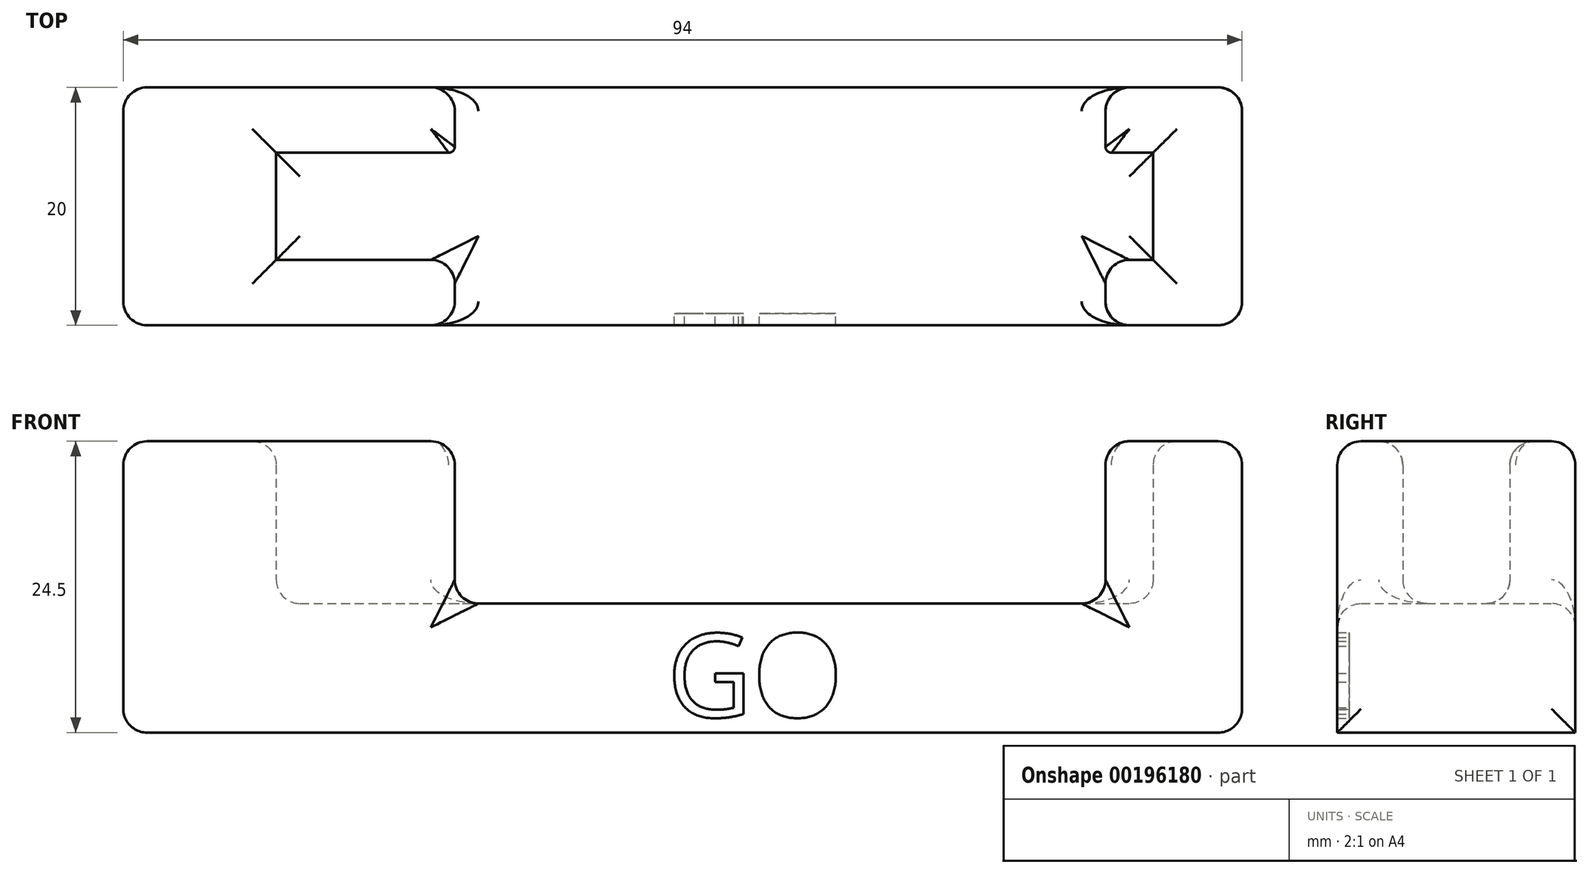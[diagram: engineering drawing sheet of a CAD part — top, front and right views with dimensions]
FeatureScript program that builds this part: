
annotation { "Feature Type Name" : "Feature", "Feature Type Description" : "" }
export const myFeature = defineFeature(function(context is Context, id is Id, definition is map)
    precondition{}
    {
        {
            var Q0;
            Q0=qCreatedBy(makeId("Front.planeOp"),FACE);
            var sketch = newSketch(context, id + "F0", { "sketchPlane" : qUnion([Q0])});
            skLineSegment(sketch, "E0.bottom", {"start": v(-9.82, 14.1) * mm, "end": v(84.18, 14.1) * mm});
            skLineSegment(sketch, "E0.left", {"start": v(-9.82, 14.1) * mm, "end": v(-9.82, -10.4) * mm});
            skLineSegment(sketch, "E0.right", {"start": v(84.18, 14.1) * mm, "end": v(84.18, -10.4) * mm});
            skLineSegment(sketch, "E1.top", {"start": v(3.03, 0.45) * mm, "end": v(76.7, 0.45) * mm});
            skLineSegment(sketch, "E1.left", {"start": v(3.03, 14.1) * mm, "end": v(3.03, 0.45) * mm});
            skLineSegment(sketch, "E1.right", {"start": v(76.7, 14.1) * mm, "end": v(76.7, 0.45) * mm});
            skText(sketch, "E2", { "text": "    GO", "fontName": "OpenSans-Regular.ttf"});
            skLineSegment(sketch, "E3", {"start": v(18.03, 14.1) * mm, "end": v(18.03, 0.45) * mm});
            skLineSegment(sketch, "E4", {"start": v(72.7, 14.1) * mm, "end": v(72.7, 0.45) * mm});
            skLineSegment(sketch, "E5", {"start": v(-9.82, -10.4) * mm, "end": v(84.18, -10.4) * mm});
            const initialGuessF0  = {"E2": [0.02568, -0.0091, 1, 0, 0.00706]};
            skSetInitialGuess(sketch, initialGuessF0);
            skSolve(sketch);
        }
        {
            var Q0;
            {var subQ3=sQuery(id+"F0.wireOp",EDGE,"E0.left");Q0=makeQuery(id+"F0.imprint","IMPRINT",FACE,{"disambiguationData":[TD([[makeQuery(id+"F0.imprint","IMPRINT",EDGE,{"derivedFrom":subQ3}),1.0]])]});}
            extrude(context, id + "F1", {"entities" : qUnion([Q0]), "depth" : 20 * mm});
        }
        {
            var Q0;
            Q0=makeQuery(id+"F0.imprint","IMPRINT",FACE,{"disambiguationData":[TD([[makeQuery(id+"F0.imprint","IMPRINT",EDGE,{"derivedFrom":sQuery(id+"F0.wireOp",EDGE,"E2.sketch_text.stroke-51")}),-1.0]])]});
            var Q1;
            Q1=makeQuery(id+"F0.imprint","IMPRINT",FACE,{"disambiguationData":[TD([[makeQuery(id+"F0.imprint","IMPRINT",EDGE,{"derivedFrom":sQuery(id+"F0.wireOp",EDGE,"E2.sketch_text.stroke-67")}),-1.0]])]});
            var Q2;
            Q2=makeQuery(id+"F0.imprint","IMPRINT",FACE,{"disambiguationData":[TD([[makeQuery(id+"F0.imprint","IMPRINT",EDGE,{"derivedFrom":sQuery(id+"F0.wireOp",EDGE,"E2.sketch_text.stroke-71")}),-1.0]])]});
            var Q3;
            Q3=makeQuery(id+"F0.imprint","IMPRINT",FACE,{"disambiguationData":[TD([[makeQuery(id+"F0.imprint","IMPRINT",EDGE,{"derivedFrom":sQuery(id+"F0.wireOp",EDGE,"E2.sketch_text.stroke-91")}),-1.0]])]});
            var Q4;
            Q4=makeQuery(id+"F0.imprint","IMPRINT",FACE,{"disambiguationData":[TD([[makeQuery(id+"F0.imprint","IMPRINT",EDGE,{"derivedFrom":sQuery(id+"F0.wireOp",EDGE,"E2.sketch_text.stroke-36")}),-1.0]])]});
            var Q5;
            Q5=makeQuery(id+"F0.imprint","IMPRINT",FACE,{"disambiguationData":[TD([[makeQuery(id+"F0.imprint","IMPRINT",EDGE,{"derivedFrom":sQuery(id+"F0.wireOp",EDGE,"E2.sketch_text.stroke-0")}),-1.0]])]});
            var Q6;
            Q6=makeQuery(id+"F0.imprint","IMPRINT",FACE,{"disambiguationData":[TD([[makeQuery(id+"F0.imprint","IMPRINT",EDGE,{"derivedFrom":sQuery(id+"F0.wireOp",EDGE,"E2.sketch_text.stroke-20")}),-1.0]])]});
            var Q7;
            Q7=makeQuery(id+"F0.imprint","IMPRINT",FACE,{"disambiguationData":[TD([[makeQuery(id+"F0.imprint","IMPRINT",EDGE,{"derivedFrom":sQuery(id+"F0.wireOp",EDGE,"E2.sketch_text.stroke-28")}),1.0]])]});
            var Q8;
            Q8=makeQuery(id+"F0.imprint","IMPRINT",FACE,{"disambiguationData":[TD([[makeQuery(id+"F0.imprint","IMPRINT",EDGE,{"derivedFrom":sQuery(id+"F0.wireOp",EDGE,"E2.sketch_text.stroke-99")}),1.0]])]});
            var Q9;
            Q9=makeQuery(id+"F0.imprint","IMPRINT",FACE,{"disambiguationData":[TD([[makeQuery(id+"F0.imprint","IMPRINT",EDGE,{"derivedFrom":sQuery(id+"F0.wireOp",EDGE,"E2.sketch_text.stroke-59")}),1.0]])]});
            extrude(context, id + "F2", {"entities" : qUnion([Q0, Q1, Q2, Q3, Q4, Q5, Q6, Q7, Q8, Q9]), "operationType" : NewBodyOperationType.ADD, "depth" : 19 * mm});
        }
        {
            var Q0;
            {var subQ0=sQuery(id+"F0.wireOp",EDGE,"E1.left");Q0=makeQuery(id+"F0.imprint","IMPRINT",FACE,{"disambiguationData":[TD([[makeQuery(id+"F0.imprint","IMPRINT",EDGE,{"derivedFrom":subQ0}),1.0]])]});}
            var Q1;
            {var subQ0=sQuery(id+"F0.wireOp",EDGE,"E1.right");Q1=makeQuery(id+"F0.imprint","IMPRINT",FACE,{"disambiguationData":[TD([[makeQuery(id+"F0.imprint","IMPRINT",EDGE,{"derivedFrom":subQ0}),-1.0]])]});}
            var Q2;
            {var subQ0=sQuery(id+"F0.wireOp",EDGE,"2L4el6af-6clv-Qu9y-48nY-g4NLMY6r5mmJ.left");Q2=makeQuery(id+"F0.imprint","IMPRINT",FACE,{"disambiguationData":[TD([[makeQuery(id+"F0.imprint","IMPRINT",EDGE,{"derivedFrom":subQ0}),1.0]])]});}
            var Q3;
            {var subQ0=sQuery(id+"F0.wireOp",EDGE,"2L4el6af-6clv-Qu9y-48nY-g4NLMY6r5mmJ.right");Q3=makeQuery(id+"F0.imprint","IMPRINT",FACE,{"disambiguationData":[TD([[makeQuery(id+"F0.imprint","IMPRINT",EDGE,{"derivedFrom":subQ0}),-1.0]])]});}
            extrude(context, id + "F3", {"entities" : qUnion([Q0, Q1, Q2, Q3]), "operationType" : NewBodyOperationType.ADD, "depth" : 20 * mm});
        }
        {
            var Q0;
            {var subQ0=sQuery(id+"F0.wireOp",EDGE,"2L4el6af-6clv-Qu9y-48nY-g4NLMY6r5mmJ.left");Q0=makeQuery(id+"F0.imprint","IMPRINT",FACE,{"disambiguationData":[TD([[makeQuery(id+"F0.imprint","IMPRINT",EDGE,{"derivedFrom":subQ0}),1.0]])]});}
            var Q1;
            {var subQ0=sQuery(id+"F0.wireOp",EDGE,"2L4el6af-6clv-Qu9y-48nY-g4NLMY6r5mmJ.right");Q1=makeQuery(id+"F0.imprint","IMPRINT",FACE,{"disambiguationData":[TD([[makeQuery(id+"F0.imprint","IMPRINT",EDGE,{"derivedFrom":subQ0}),-1.0]])]});}
            var Q2;
            {var subQ0=sQuery(id+"F0.wireOp",EDGE,"E1.left");Q2=makeQuery(id+"F0.imprint","IMPRINT",FACE,{"disambiguationData":[TD([[makeQuery(id+"F0.imprint","IMPRINT",EDGE,{"derivedFrom":subQ0}),1.0]])]});}
            var Q3;
            {var subQ0=sQuery(id+"F0.wireOp",EDGE,"E1.right");Q3=makeQuery(id+"F0.imprint","IMPRINT",FACE,{"disambiguationData":[TD([[makeQuery(id+"F0.imprint","IMPRINT",EDGE,{"derivedFrom":subQ0}),-1.0]])]});}
            extrude(context, id + "F4", {"entities" : qUnion([Q0, Q1, Q2, Q3]), "operationType" : NewBodyOperationType.REMOVE, "depth" : 14.5 * mm, "hasSecondDirection" : true, "secondDirectionOppositeDirection" : false, "secondDirectionDepth" : 5.5 * mm});
        }
        {
            var Q0;
            Q0=makeQuery(id+"F4.boolean.opBoolean","COPY",EDGE,{"derivedFrom":makeQuery(id+"F4.opExtrude","SWEPT_EDGE",EDGE,{"disambiguationData":[OSD([sQuery(id+"F0.wireOp",EDGE,"E0.top"),sQuery(id+"F0.wireOp",EDGE,"2L4el6af-6clv-Qu9y-48nY-g4NLMY6r5mmJ.left")])]})});
            var Q1;
            {var subQ0=sQuery(id+"F0.wireOp",EDGE,"E0.top");Q1=makeQuery(id+"F4.boolean.opBoolean","COPY",EDGE,{"derivedFrom":makeQuery(id+"F4.opExtrude","CAP_EDGE",EDGE,{"disambiguationData":[OSD([subQ0]),TDD([makeQuery(id+"F0.imprint","IMPRINT",EDGE,{"disambiguationData":[TD([[makeQuery(id+"F0.imprint","INTERSECT",VERTEX,{"derivedFrom":[subQ0,sQuery(id+"F0.wireOp",EDGE,"2L4el6af-6clv-Qu9y-48nY-g4NLMY6r5mmJ.left")]}),-1.0]])],"derivedFrom":subQ0})])],"isStart":false})});}
            var Q2;
            {var subQ0=sQuery(id+"F0.wireOp",EDGE,"E0.top");Q2=makeQuery(id+"F4.boolean.opBoolean","COPY",EDGE,{"derivedFrom":makeQuery(id+"F4.opExtrude","CAP_EDGE",EDGE,{"disambiguationData":[OSD([subQ0]),TDD([makeQuery(id+"F0.imprint","IMPRINT",EDGE,{"disambiguationData":[TD([[makeQuery(id+"F0.imprint","INTERSECT",VERTEX,{"derivedFrom":[subQ0,sQuery(id+"F0.wireOp",EDGE,"2L4el6af-6clv-Qu9y-48nY-g4NLMY6r5mmJ.left")]}),-1.0]])],"derivedFrom":subQ0})])],"isStart":true})});}
            var Q3;
            Q3=makeQuery(id+"F4.boolean.opBoolean","COPY",EDGE,{"derivedFrom":makeQuery(id+"F4.opExtrude","CAP_EDGE",EDGE,{"disambiguationData":[OSD([sQuery(id+"F0.wireOp",EDGE,"ZneDm9bx-5IyB-59Bp-oYEK-Q0VNZlboGKRZ")])],"isStart":false})});
            var Q4;
            Q4=makeQuery(id+"F4.boolean.opBoolean","COPY",EDGE,{"derivedFrom":makeQuery(id+"F4.opExtrude","CAP_EDGE",EDGE,{"disambiguationData":[OSD([sQuery(id+"F0.wireOp",EDGE,"ZneDm9bx-5IyB-59Bp-oYEK-Q0VNZlboGKRZ")])],"isStart":true})});
            var Q5;
            {var subQ0=sQuery(id+"F0.wireOp",EDGE,"E0.top");Q5=makeQuery(id+"F4.boolean.opBoolean","COPY",EDGE,{"derivedFrom":makeQuery(id+"F4.opExtrude","CAP_EDGE",EDGE,{"disambiguationData":[OSD([subQ0]),TDD([makeQuery(id+"F0.imprint","IMPRINT",EDGE,{"disambiguationData":[TD([[makeQuery(id+"F0.imprint","INTERSECT",VERTEX,{"derivedFrom":[subQ0,sQuery(id+"F0.wireOp",EDGE,"2L4el6af-6clv-Qu9y-48nY-g4NLMY6r5mmJ.right")]}),1.0]])],"derivedFrom":subQ0})])],"isStart":false})});}
            var Q6;
            Q6=makeQuery(id+"F4.boolean.opBoolean","COPY",EDGE,{"derivedFrom":makeQuery(id+"F4.opExtrude","SWEPT_EDGE",EDGE,{"disambiguationData":[OSD([sQuery(id+"F0.wireOp",EDGE,"E0.top"),sQuery(id+"F0.wireOp",EDGE,"2L4el6af-6clv-Qu9y-48nY-g4NLMY6r5mmJ.right")])]})});
            var Q7;
            {var subQ0=sQuery(id+"F0.wireOp",EDGE,"E0.top");Q7=makeQuery(id+"F4.boolean.opBoolean","COPY",EDGE,{"derivedFrom":makeQuery(id+"F4.opExtrude","CAP_EDGE",EDGE,{"disambiguationData":[OSD([subQ0]),TDD([makeQuery(id+"F0.imprint","IMPRINT",EDGE,{"disambiguationData":[TD([[makeQuery(id+"F0.imprint","INTERSECT",VERTEX,{"derivedFrom":[subQ0,sQuery(id+"F0.wireOp",EDGE,"2L4el6af-6clv-Qu9y-48nY-g4NLMY6r5mmJ.right")]}),1.0]])],"derivedFrom":subQ0})])],"isStart":true})});}
            var Q8;
            Q8=makeQuery(id+"F4.boolean.opBoolean","COPY",EDGE,{"derivedFrom":makeQuery(id+"F4.opExtrude","CAP_EDGE",EDGE,{"disambiguationData":[OSD([sQuery(id+"F0.wireOp",EDGE,"gIBaWbCc-atec-Ogfb-776C-qDHbfGT0BQME")])],"isStart":true})});
            var Q9;
            Q9=makeQuery(id+"F4.boolean.opBoolean","COPY",EDGE,{"derivedFrom":makeQuery(id+"F4.opExtrude","CAP_EDGE",EDGE,{"disambiguationData":[OSD([sQuery(id+"F0.wireOp",EDGE,"gIBaWbCc-atec-Ogfb-776C-qDHbfGT0BQME")])],"isStart":false})});
            var Q10;
            {var subQ0=sQuery(id+"F0.wireOp",EDGE,"E0.bottom");Q10=makeQuery(id+"F4.boolean.opBoolean","COPY",EDGE,{"derivedFrom":makeQuery(id+"F4.opExtrude","CAP_EDGE",EDGE,{"disambiguationData":[OSD([subQ0]),TDD([makeQuery(id+"F0.imprint","IMPRINT",EDGE,{"disambiguationData":[TD([[makeQuery(id+"F0.imprint","INTERSECT",VERTEX,{"derivedFrom":[subQ0,sQuery(id+"F0.wireOp",EDGE,"E1.left")]}),-1.0]])],"derivedFrom":subQ0})])],"isStart":true})});}
            var Q11;
            Q11=makeQuery(id+"F4.boolean.opBoolean","COPY",EDGE,{"derivedFrom":makeQuery(id+"F4.opExtrude","SWEPT_EDGE",EDGE,{"disambiguationData":[OSD([sQuery(id+"F0.wireOp",EDGE,"E0.bottom"),sQuery(id+"F0.wireOp",EDGE,"E1.left")])]})});
            var Q12;
            {var subQ0=sQuery(id+"F0.wireOp",EDGE,"E0.bottom");Q12=makeQuery(id+"F4.boolean.opBoolean","COPY",EDGE,{"derivedFrom":makeQuery(id+"F4.opExtrude","CAP_EDGE",EDGE,{"disambiguationData":[OSD([subQ0]),TDD([makeQuery(id+"F0.imprint","IMPRINT",EDGE,{"disambiguationData":[TD([[makeQuery(id+"F0.imprint","INTERSECT",VERTEX,{"derivedFrom":[subQ0,sQuery(id+"F0.wireOp",EDGE,"E1.left")]}),-1.0]])],"derivedFrom":subQ0})])],"isStart":false})});}
            var Q13;
            {var subQ0=sQuery(id+"F0.wireOp",EDGE,"E0.bottom");Q13=makeQuery(id+"F4.boolean.opBoolean","COPY",EDGE,{"derivedFrom":makeQuery(id+"F4.opExtrude","CAP_EDGE",EDGE,{"disambiguationData":[OSD([subQ0]),TDD([makeQuery(id+"F0.imprint","IMPRINT",EDGE,{"disambiguationData":[TD([[makeQuery(id+"F0.imprint","INTERSECT",VERTEX,{"derivedFrom":[subQ0,sQuery(id+"F0.wireOp",EDGE,"E1.right")]}),1.0]])],"derivedFrom":subQ0})])],"isStart":true})});}
            var Q14;
            Q14=makeQuery(id+"F4.boolean.opBoolean","COPY",EDGE,{"derivedFrom":makeQuery(id+"F4.opExtrude","SWEPT_EDGE",EDGE,{"disambiguationData":[OSD([sQuery(id+"F0.wireOp",EDGE,"E0.bottom"),sQuery(id+"F0.wireOp",EDGE,"E1.right")])]})});
            var Q15;
            {var subQ0=sQuery(id+"F0.wireOp",EDGE,"E0.bottom");Q15=makeQuery(id+"F4.boolean.opBoolean","COPY",EDGE,{"derivedFrom":makeQuery(id+"F4.opExtrude","CAP_EDGE",EDGE,{"disambiguationData":[OSD([subQ0]),TDD([makeQuery(id+"F0.imprint","IMPRINT",EDGE,{"disambiguationData":[TD([[makeQuery(id+"F0.imprint","INTERSECT",VERTEX,{"derivedFrom":[subQ0,sQuery(id+"F0.wireOp",EDGE,"E1.right")]}),1.0]])],"derivedFrom":subQ0})])],"isStart":false})});}
            var Q16;
            Q16=makeQuery(id+"F4.boolean.opBoolean","COPY",EDGE,{"derivedFrom":makeQuery(id+"F4.opExtrude","CAP_EDGE",EDGE,{"disambiguationData":[OSD([sQuery(id+"F0.wireOp",EDGE,"E3")])],"isStart":true})});
            var Q17;
            Q17=makeQuery(id+"F4.boolean.opBoolean","COPY",EDGE,{"derivedFrom":makeQuery(id+"F4.opExtrude","CAP_EDGE",EDGE,{"disambiguationData":[OSD([sQuery(id+"F0.wireOp",EDGE,"E3")])],"isStart":false})});
            var Q18;
            Q18=makeQuery(id+"F4.boolean.opBoolean","COPY",EDGE,{"derivedFrom":makeQuery(id+"F4.opExtrude","CAP_EDGE",EDGE,{"disambiguationData":[OSD([sQuery(id+"F0.wireOp",EDGE,"E4")])],"isStart":true})});
            var Q19;
            Q19=makeQuery(id+"F4.boolean.opBoolean","COPY",EDGE,{"derivedFrom":makeQuery(id+"F4.opExtrude","CAP_EDGE",EDGE,{"disambiguationData":[OSD([sQuery(id+"F0.wireOp",EDGE,"E4")])],"isStart":false})});
            fillet(context, id + "F5", {"entities" : qUnion([Q0, Q1, Q2, Q3, Q4, Q5, Q6, Q7, Q8, Q9, Q10, Q11, Q12, Q13, Q14, Q15, Q16, Q17, Q18, Q19]), "radius" : 0.5 * mm, "tangentPropagation" : true, "allowEdgeOverflow" : false});
        }
        {
            var Q0;
            {var subQ0=sQuery(id+"F0.wireOp",EDGE,"E0.bottom");var subQ1=makeQuery(id+"F0.imprint","INTERSECT",VERTEX,{"derivedFrom":[subQ0,sQuery(id+"F0.wireOp",EDGE,"E1.left")]});Q0=makeQuery(id+"F3.boolean.opBoolean","MERGE",EDGE,{"derivedFrom":[makeQuery(id+"F1.opExtrude","CAP_EDGE",EDGE,{"disambiguationData":[OSD([subQ0]),TDD([makeQuery(id+"F0.imprint","IMPRINT",EDGE,{"disambiguationData":[TD([[makeQuery(id+"F0.imprint","INTERSECT",VERTEX,{"derivedFrom":[subQ0,sQuery(id+"F0.wireOp",EDGE,"E0.left")]}),-1.0]])],"derivedFrom":subQ0})])],"isStart":true}),makeQuery(id+"F3.opExtrude","CAP_EDGE",EDGE,{"disambiguationData":[OSD([subQ0]),TDD([makeQuery(id+"F0.imprint","IMPRINT",EDGE,{"disambiguationData":[TD([[subQ1,-1.0]])],"derivedFrom":subQ0})])],"isStart":true})]});}
            var Q1;
            Q1=makeQuery(id+"F1.opExtrude","SWEPT_EDGE",EDGE,{"disambiguationData":[OSD([sQuery(id+"F0.wireOp",EDGE,"E0.bottom"),sQuery(id+"F0.wireOp",EDGE,"E0.left")])]});
            var Q2;
            {var subQ0=sQuery(id+"F0.wireOp",EDGE,"E0.bottom");var subQ1=makeQuery(id+"F0.imprint","INTERSECT",VERTEX,{"derivedFrom":[subQ0,sQuery(id+"F0.wireOp",EDGE,"E1.left")]});Q2=makeQuery(id+"F3.boolean.opBoolean","MERGE",EDGE,{"derivedFrom":[makeQuery(id+"F1.opExtrude","CAP_EDGE",EDGE,{"disambiguationData":[OSD([subQ0]),TDD([makeQuery(id+"F0.imprint","IMPRINT",EDGE,{"disambiguationData":[TD([[makeQuery(id+"F0.imprint","INTERSECT",VERTEX,{"derivedFrom":[subQ0,sQuery(id+"F0.wireOp",EDGE,"E0.left")]}),-1.0]])],"derivedFrom":subQ0})])],"isStart":false}),makeQuery(id+"F3.opExtrude","CAP_EDGE",EDGE,{"disambiguationData":[OSD([subQ0]),TDD([makeQuery(id+"F0.imprint","IMPRINT",EDGE,{"disambiguationData":[TD([[subQ1,-1.0]])],"derivedFrom":subQ0})])],"isStart":false})]});}
            var Q3;
            Q3=makeQuery(id+"F1.opExtrude","CAP_EDGE",EDGE,{"disambiguationData":[OSD([sQuery(id+"F0.wireOp",EDGE,"E1.top")])],"isStart":false});
            var Q4;
            Q4=makeQuery(id+"F1.opExtrude","CAP_EDGE",EDGE,{"disambiguationData":[OSD([sQuery(id+"F0.wireOp",EDGE,"E1.top")])],"isStart":true});
            var Q5;
            {var subQ0=sQuery(id+"F0.wireOp",EDGE,"E0.bottom");var subQ1=makeQuery(id+"F0.imprint","INTERSECT",VERTEX,{"derivedFrom":[subQ0,sQuery(id+"F0.wireOp",EDGE,"E1.right")]});Q5=makeQuery(id+"F3.boolean.opBoolean","MERGE",EDGE,{"derivedFrom":[makeQuery(id+"F1.opExtrude","CAP_EDGE",EDGE,{"disambiguationData":[OSD([subQ0]),TDD([makeQuery(id+"F0.imprint","IMPRINT",EDGE,{"disambiguationData":[TD([[makeQuery(id+"F0.imprint","INTERSECT",VERTEX,{"derivedFrom":[subQ0,sQuery(id+"F0.wireOp",EDGE,"E0.right")]}),1.0]])],"derivedFrom":subQ0})])],"isStart":true}),makeQuery(id+"F3.opExtrude","CAP_EDGE",EDGE,{"disambiguationData":[OSD([subQ0]),TDD([makeQuery(id+"F0.imprint","IMPRINT",EDGE,{"disambiguationData":[TD([[subQ1,1.0]])],"derivedFrom":subQ0})])],"isStart":true})]});}
            var Q6;
            Q6=makeQuery(id+"F1.opExtrude","SWEPT_EDGE",EDGE,{"disambiguationData":[OSD([sQuery(id+"F0.wireOp",EDGE,"E0.bottom"),sQuery(id+"F0.wireOp",EDGE,"E0.right")])]});
            var Q7;
            {var subQ0=sQuery(id+"F0.wireOp",EDGE,"E0.bottom");var subQ1=makeQuery(id+"F0.imprint","INTERSECT",VERTEX,{"derivedFrom":[subQ0,sQuery(id+"F0.wireOp",EDGE,"E1.right")]});Q7=makeQuery(id+"F3.boolean.opBoolean","MERGE",EDGE,{"derivedFrom":[makeQuery(id+"F1.opExtrude","CAP_EDGE",EDGE,{"disambiguationData":[OSD([subQ0]),TDD([makeQuery(id+"F0.imprint","IMPRINT",EDGE,{"disambiguationData":[TD([[makeQuery(id+"F0.imprint","INTERSECT",VERTEX,{"derivedFrom":[subQ0,sQuery(id+"F0.wireOp",EDGE,"E0.right")]}),1.0]])],"derivedFrom":subQ0})])],"isStart":false}),makeQuery(id+"F3.opExtrude","CAP_EDGE",EDGE,{"disambiguationData":[OSD([subQ0]),TDD([makeQuery(id+"F0.imprint","IMPRINT",EDGE,{"disambiguationData":[TD([[subQ1,1.0]])],"derivedFrom":subQ0})])],"isStart":false})]});}
            var Q8;
            {var subQ4=sQuery(id+"F0.wireOp",EDGE,"E1.left");var subQ5=sQuery(id+"F0.wireOp",EDGE,"E1.top");var subQ8=sQuery(id+"F0.wireOp",EDGE,"E0.bottom");var subQ9=sQuery(id+"F0.wireOp",EDGE,"E3");Q8=makeQuery(id+"F4.boolean.opBoolean","SPLIT",EDGE,{"disambiguationData":[TD([makeQuery(id+"F3.opExtrude","CAP_FACE",FACE,{"disambiguationData":[OSD([subQ8,subQ5,subQ4,subQ9])],"isStart":false})])],"derivedFrom":makeQuery(id+"F3.opExtrude","SWEPT_EDGE",EDGE,{"disambiguationData":[OSD([subQ8,subQ9])]})});}
            var Q9;
            {var subQ1=sQuery(id+"F0.wireOp",EDGE,"E0.bottom");var subQ3=sQuery(id+"F0.wireOp",EDGE,"E3");var subQ36=sQuery(id+"F0.wireOp",EDGE,"E2.sketch_text.stroke-70");var subQ37=sQuery(id+"F0.wireOp",EDGE,"E2.sketch_text.stroke-69");var subQ38=sQuery(id+"F0.wireOp",EDGE,"E2.sketch_text.stroke-68");var subQ39=sQuery(id+"F0.wireOp",EDGE,"E2.sketch_text.stroke-67");Q9=makeQuery(id+"F4.boolean.opBoolean","SPLIT",EDGE,{"disambiguationData":[TD([makeQuery(id+"F2.opExtrude","CAP_FACE",FACE,{"disambiguationData":[OSD([subQ39,subQ38,subQ37,subQ36])],"isStart":true})])],"derivedFrom":makeQuery(id+"F3.opExtrude","SWEPT_EDGE",EDGE,{"disambiguationData":[OSD([subQ1,subQ3])]})});}
            var Q10;
            {var subQ2=sQuery(id+"F0.wireOp",EDGE,"E0.bottom");var subQ3=sQuery(id+"F0.wireOp",EDGE,"E4");var subQ33=sQuery(id+"F0.wireOp",EDGE,"E2.sketch_text.stroke-70");var subQ34=sQuery(id+"F0.wireOp",EDGE,"E2.sketch_text.stroke-69");var subQ35=sQuery(id+"F0.wireOp",EDGE,"E2.sketch_text.stroke-68");var subQ36=sQuery(id+"F0.wireOp",EDGE,"E2.sketch_text.stroke-67");Q10=makeQuery(id+"F4.boolean.opBoolean","SPLIT",EDGE,{"disambiguationData":[TD([makeQuery(id+"F2.opExtrude","CAP_FACE",FACE,{"disambiguationData":[OSD([subQ36,subQ35,subQ34,subQ33])],"isStart":true})])],"derivedFrom":makeQuery(id+"F3.opExtrude","SWEPT_EDGE",EDGE,{"disambiguationData":[OSD([subQ2,subQ3])]})});}
            var Q11;
            Q11=makeQuery(id+"F3.opExtrude","CAP_EDGE",EDGE,{"disambiguationData":[OSD([sQuery(id+"F0.wireOp",EDGE,"E4")])],"isStart":false});
            var Q12;
            {var subQ1=sQuery(id+"F0.wireOp",EDGE,"E0.bottom");var subQ3=sQuery(id+"F0.wireOp",EDGE,"E4");var subQ4=sQuery(id+"F0.wireOp",EDGE,"E1.left");var subQ5=sQuery(id+"F0.wireOp",EDGE,"E1.top");Q12=makeQuery(id+"F4.boolean.opBoolean","SPLIT",EDGE,{"disambiguationData":[TD([makeQuery(id+"F3.opExtrude","CAP_FACE",FACE,{"disambiguationData":[OSD([subQ1,subQ5,subQ4,sQuery(id+"F0.wireOp",EDGE,"E3")])],"isStart":false})])],"derivedFrom":makeQuery(id+"F3.opExtrude","SWEPT_EDGE",EDGE,{"disambiguationData":[OSD([subQ1,subQ3])]})});}
            var Q13;
            Q13=makeQuery(id+"F3.opExtrude","CAP_EDGE",EDGE,{"disambiguationData":[OSD([sQuery(id+"F0.wireOp",EDGE,"E4")])],"isStart":true});
            var Q14;
            Q14=makeQuery(id+"F3.opExtrude","CAP_EDGE",EDGE,{"disambiguationData":[OSD([sQuery(id+"F0.wireOp",EDGE,"E3")])],"isStart":false});
            var Q15;
            Q15=makeQuery(id+"F3.opExtrude","CAP_EDGE",EDGE,{"disambiguationData":[OSD([sQuery(id+"F0.wireOp",EDGE,"E3")])],"isStart":true});
            var Q16;
            {var subQ0=sQuery(id+"F0.wireOp",EDGE,"E0.top");var subQ1=makeQuery(id+"F0.imprint","INTERSECT",VERTEX,{"derivedFrom":[subQ0,sQuery(id+"F0.wireOp",EDGE,"2L4el6af-6clv-Qu9y-48nY-g4NLMY6r5mmJ.left")]});Q16=makeQuery(id+"F3.boolean.opBoolean","MERGE",EDGE,{"derivedFrom":[makeQuery(id+"F1.opExtrude","CAP_EDGE",EDGE,{"disambiguationData":[OSD([subQ0]),TDD([makeQuery(id+"F0.imprint","IMPRINT",EDGE,{"disambiguationData":[TD([[makeQuery(id+"F0.imprint","INTERSECT",VERTEX,{"derivedFrom":[subQ0,sQuery(id+"F0.wireOp",EDGE,"E0.left")]}),-1.0]])],"derivedFrom":subQ0})])],"isStart":false}),makeQuery(id+"F3.opExtrude","CAP_EDGE",EDGE,{"disambiguationData":[OSD([subQ0]),TDD([makeQuery(id+"F0.imprint","IMPRINT",EDGE,{"disambiguationData":[TD([[subQ1,-1.0]])],"derivedFrom":subQ0})])],"isStart":false})]});}
            var Q17;
            Q17=makeQuery(id+"F1.opExtrude","CAP_EDGE",EDGE,{"disambiguationData":[OSD([sQuery(id+"F0.wireOp",EDGE,"2L4el6af-6clv-Qu9y-48nY-g4NLMY6r5mmJ.bottom")])],"isStart":false});
            var Q18;
            Q18=makeQuery(id+"F3.opExtrude","CAP_EDGE",EDGE,{"disambiguationData":[OSD([sQuery(id+"F0.wireOp",EDGE,"gIBaWbCc-atec-Ogfb-776C-qDHbfGT0BQME")])],"isStart":false});
            var Q19;
            {var subQ0=sQuery(id+"F0.wireOp",EDGE,"E1.left");var subQ1=sQuery(id+"F0.wireOp",EDGE,"E1.top");var subQ2=sQuery(id+"F0.wireOp",EDGE,"E0.bottom");var subQ3=sQuery(id+"F0.wireOp",EDGE,"gIBaWbCc-atec-Ogfb-776C-qDHbfGT0BQME");var subQ6=sQuery(id+"F0.wireOp",EDGE,"E0.top");Q19=makeQuery(id+"F4.boolean.opBoolean","SPLIT",EDGE,{"disambiguationData":[TD([makeQuery(id+"F3.opExtrude","CAP_FACE",FACE,{"disambiguationData":[OSD([subQ2,subQ1,subQ0,sQuery(id+"F0.wireOp",EDGE,"E3")])],"isStart":false})])],"derivedFrom":makeQuery(id+"F3.opExtrude","SWEPT_EDGE",EDGE,{"disambiguationData":[OSD([subQ6,subQ3])]})});}
            var Q20;
            {var subQ0=sQuery(id+"F0.wireOp",EDGE,"E0.top");var subQ1=makeQuery(id+"F0.imprint","INTERSECT",VERTEX,{"derivedFrom":[subQ0,sQuery(id+"F0.wireOp",EDGE,"2L4el6af-6clv-Qu9y-48nY-g4NLMY6r5mmJ.right")]});Q20=makeQuery(id+"F3.boolean.opBoolean","MERGE",EDGE,{"derivedFrom":[makeQuery(id+"F1.opExtrude","CAP_EDGE",EDGE,{"disambiguationData":[OSD([subQ0]),TDD([makeQuery(id+"F0.imprint","IMPRINT",EDGE,{"disambiguationData":[TD([[makeQuery(id+"F0.imprint","INTERSECT",VERTEX,{"derivedFrom":[subQ0,sQuery(id+"F0.wireOp",EDGE,"E0.right")]}),1.0]])],"derivedFrom":subQ0})])],"isStart":false}),makeQuery(id+"F3.opExtrude","CAP_EDGE",EDGE,{"disambiguationData":[OSD([subQ0]),TDD([makeQuery(id+"F0.imprint","IMPRINT",EDGE,{"disambiguationData":[TD([[subQ1,1.0]])],"derivedFrom":subQ0})])],"isStart":false})]});}
            var Q21;
            Q21=makeQuery(id+"F1.opExtrude","SWEPT_EDGE",EDGE,{"disambiguationData":[OSD([sQuery(id+"F0.wireOp",EDGE,"E0.top"),sQuery(id+"F0.wireOp",EDGE,"E0.right")])]});
            var Q22;
            {var subQ0=sQuery(id+"F0.wireOp",EDGE,"E0.top");var subQ1=makeQuery(id+"F0.imprint","INTERSECT",VERTEX,{"derivedFrom":[subQ0,sQuery(id+"F0.wireOp",EDGE,"2L4el6af-6clv-Qu9y-48nY-g4NLMY6r5mmJ.right")]});Q22=makeQuery(id+"F3.boolean.opBoolean","MERGE",EDGE,{"derivedFrom":[makeQuery(id+"F1.opExtrude","CAP_EDGE",EDGE,{"disambiguationData":[OSD([subQ0]),TDD([makeQuery(id+"F0.imprint","IMPRINT",EDGE,{"disambiguationData":[TD([[makeQuery(id+"F0.imprint","INTERSECT",VERTEX,{"derivedFrom":[subQ0,sQuery(id+"F0.wireOp",EDGE,"E0.right")]}),1.0]])],"derivedFrom":subQ0})])],"isStart":true}),makeQuery(id+"F3.opExtrude","CAP_EDGE",EDGE,{"disambiguationData":[OSD([subQ0]),TDD([makeQuery(id+"F0.imprint","IMPRINT",EDGE,{"disambiguationData":[TD([[subQ1,1.0]])],"derivedFrom":subQ0})])],"isStart":true})]});}
            var Q23;
            {var subQ32=sQuery(id+"F0.wireOp",EDGE,"E0.top");var subQ35=sQuery(id+"F0.wireOp",EDGE,"E2.sketch_text.stroke-70");var subQ36=sQuery(id+"F0.wireOp",EDGE,"E2.sketch_text.stroke-69");var subQ37=sQuery(id+"F0.wireOp",EDGE,"E2.sketch_text.stroke-68");var subQ38=sQuery(id+"F0.wireOp",EDGE,"E2.sketch_text.stroke-67");var subQ47=sQuery(id+"F0.wireOp",EDGE,"gIBaWbCc-atec-Ogfb-776C-qDHbfGT0BQME");Q23=makeQuery(id+"F4.boolean.opBoolean","SPLIT",EDGE,{"disambiguationData":[TD([makeQuery(id+"F2.opExtrude","CAP_FACE",FACE,{"disambiguationData":[OSD([subQ38,subQ37,subQ36,subQ35])],"isStart":true})])],"derivedFrom":makeQuery(id+"F3.opExtrude","SWEPT_EDGE",EDGE,{"disambiguationData":[OSD([subQ32,subQ47])]})});}
            var Q24;
            Q24=makeQuery(id+"F3.opExtrude","CAP_EDGE",EDGE,{"disambiguationData":[OSD([sQuery(id+"F0.wireOp",EDGE,"gIBaWbCc-atec-Ogfb-776C-qDHbfGT0BQME")])],"isStart":true});
            var Q25;
            Q25=makeQuery(id+"F1.opExtrude","CAP_EDGE",EDGE,{"disambiguationData":[OSD([sQuery(id+"F0.wireOp",EDGE,"2L4el6af-6clv-Qu9y-48nY-g4NLMY6r5mmJ.bottom")])],"isStart":true});
            var Q26;
            {var subQ0=sQuery(id+"F0.wireOp",EDGE,"E1.left");var subQ1=sQuery(id+"F0.wireOp",EDGE,"E1.top");var subQ2=sQuery(id+"F0.wireOp",EDGE,"E0.bottom");var subQ3=sQuery(id+"F0.wireOp",EDGE,"ZneDm9bx-5IyB-59Bp-oYEK-Q0VNZlboGKRZ");var subQ6=sQuery(id+"F0.wireOp",EDGE,"E0.top");Q26=makeQuery(id+"F4.boolean.opBoolean","SPLIT",EDGE,{"disambiguationData":[TD([makeQuery(id+"F3.opExtrude","CAP_FACE",FACE,{"disambiguationData":[OSD([subQ2,subQ1,subQ0,sQuery(id+"F0.wireOp",EDGE,"E3")])],"isStart":false})])],"derivedFrom":makeQuery(id+"F3.opExtrude","SWEPT_EDGE",EDGE,{"disambiguationData":[OSD([subQ6,subQ3])]})});}
            var Q27;
            Q27=makeQuery(id+"F3.opExtrude","CAP_EDGE",EDGE,{"disambiguationData":[OSD([sQuery(id+"F0.wireOp",EDGE,"ZneDm9bx-5IyB-59Bp-oYEK-Q0VNZlboGKRZ")])],"isStart":false});
            var Q28;
            {var subQ28=sQuery(id+"F0.wireOp",EDGE,"ZneDm9bx-5IyB-59Bp-oYEK-Q0VNZlboGKRZ");var subQ31=sQuery(id+"F0.wireOp",EDGE,"E0.top");var subQ32=sQuery(id+"F0.wireOp",EDGE,"E2.sketch_text.stroke-70");var subQ33=sQuery(id+"F0.wireOp",EDGE,"E2.sketch_text.stroke-69");var subQ34=sQuery(id+"F0.wireOp",EDGE,"E2.sketch_text.stroke-68");var subQ35=sQuery(id+"F0.wireOp",EDGE,"E2.sketch_text.stroke-67");Q28=makeQuery(id+"F4.boolean.opBoolean","SPLIT",EDGE,{"disambiguationData":[TD([makeQuery(id+"F2.opExtrude","CAP_FACE",FACE,{"disambiguationData":[OSD([subQ35,subQ34,subQ33,subQ32])],"isStart":true})])],"derivedFrom":makeQuery(id+"F3.opExtrude","SWEPT_EDGE",EDGE,{"disambiguationData":[OSD([subQ31,subQ28])]})});}
            var Q29;
            {var subQ0=sQuery(id+"F0.wireOp",EDGE,"E0.top");var subQ1=makeQuery(id+"F0.imprint","INTERSECT",VERTEX,{"derivedFrom":[subQ0,sQuery(id+"F0.wireOp",EDGE,"2L4el6af-6clv-Qu9y-48nY-g4NLMY6r5mmJ.left")]});Q29=makeQuery(id+"F3.boolean.opBoolean","MERGE",EDGE,{"derivedFrom":[makeQuery(id+"F1.opExtrude","CAP_EDGE",EDGE,{"disambiguationData":[OSD([subQ0]),TDD([makeQuery(id+"F0.imprint","IMPRINT",EDGE,{"disambiguationData":[TD([[makeQuery(id+"F0.imprint","INTERSECT",VERTEX,{"derivedFrom":[subQ0,sQuery(id+"F0.wireOp",EDGE,"E0.left")]}),-1.0]])],"derivedFrom":subQ0})])],"isStart":true}),makeQuery(id+"F3.opExtrude","CAP_EDGE",EDGE,{"disambiguationData":[OSD([subQ0]),TDD([makeQuery(id+"F0.imprint","IMPRINT",EDGE,{"disambiguationData":[TD([[subQ1,-1.0]])],"derivedFrom":subQ0})])],"isStart":true})]});}
            var Q30;
            Q30=makeQuery(id+"F1.opExtrude","SWEPT_EDGE",EDGE,{"disambiguationData":[OSD([sQuery(id+"F0.wireOp",EDGE,"E0.top"),sQuery(id+"F0.wireOp",EDGE,"E0.left")])]});
            var Q31;
            Q31=makeQuery(id+"F1.opExtrude","SWEPT_FACE",FACE,{"disambiguationData":[OSD([sQuery(id+"F0.wireOp",EDGE,"E0.right")])]});
            var Q32;
            Q32=makeQuery(id+"F1.opExtrude","SWEPT_FACE",FACE,{"disambiguationData":[OSD([sQuery(id+"F0.wireOp",EDGE,"E0.left")])]});
            fillet(context, id + "F6", {"entities" : qUnion([Q0, Q1, Q2, Q3, Q4, Q5, Q6, Q7, Q8, Q9, Q10, Q11, Q12, Q13, Q14, Q15, Q16, Q17, Q18, Q19, Q20, Q21, Q22, Q23, Q24, Q25, Q26, Q27, Q28, Q29, Q30, Q31, Q32]), "radius" : 2 * mm, "tangentPropagation" : true, "allowEdgeOverflow" : false});
        }
        {
            var Q0;
            {var subQ2=sQuery(id+"F0.wireOp",EDGE,"E1.top");var subQ3=sQuery(id+"F0.wireOp",EDGE,"E0.bottom");var subQ4=sQuery(id+"F0.wireOp",EDGE,"E3");var subQ5=sQuery(id+"F0.wireOp",EDGE,"E1.left");Q0=makeQuery(id+"F4.boolean.opBoolean","SPLIT",EDGE,{"disambiguationData":[TD([makeQuery(id+"F3.opExtrude","CAP_FACE",FACE,{"disambiguationData":[OSD([subQ3,subQ2,subQ5,subQ4])],"isStart":false})])],"derivedFrom":makeQuery(id+"F3.opExtrude","SWEPT_EDGE",EDGE,{"disambiguationData":[OSD([subQ2,subQ4])]})});}
            var Q1;
            {var subQ0=sQuery(id+"F0.wireOp",EDGE,"E3");var subQ2=sQuery(id+"F0.wireOp",EDGE,"E1.top");var subQ32=sQuery(id+"F0.wireOp",EDGE,"E2.sketch_text.stroke-70");var subQ33=sQuery(id+"F0.wireOp",EDGE,"E2.sketch_text.stroke-69");var subQ34=sQuery(id+"F0.wireOp",EDGE,"E2.sketch_text.stroke-68");var subQ35=sQuery(id+"F0.wireOp",EDGE,"E2.sketch_text.stroke-67");Q1=makeQuery(id+"F4.boolean.opBoolean","SPLIT",EDGE,{"disambiguationData":[TD([makeQuery(id+"F2.opExtrude","CAP_FACE",FACE,{"disambiguationData":[OSD([subQ35,subQ34,subQ33,subQ32])],"isStart":true})])],"derivedFrom":makeQuery(id+"F3.opExtrude","SWEPT_EDGE",EDGE,{"disambiguationData":[OSD([subQ2,subQ0])]})});}
            var Q2;
            {var subQ1=sQuery(id+"F0.wireOp",EDGE,"E1.top");var subQ2=sQuery(id+"F0.wireOp",EDGE,"E0.bottom");var subQ3=sQuery(id+"F0.wireOp",EDGE,"E1.left");var subQ4=sQuery(id+"F0.wireOp",EDGE,"ZneDm9bx-5IyB-59Bp-oYEK-Q0VNZlboGKRZ");var subQ5=sQuery(id+"F0.wireOp",EDGE,"2L4el6af-6clv-Qu9y-48nY-g4NLMY6r5mmJ.bottom");Q2=makeQuery(id+"F4.boolean.opBoolean","SPLIT",EDGE,{"disambiguationData":[TD([makeQuery(id+"F3.opExtrude","CAP_FACE",FACE,{"disambiguationData":[OSD([subQ2,subQ1,subQ3,sQuery(id+"F0.wireOp",EDGE,"E3")])],"isStart":false})])],"derivedFrom":makeQuery(id+"F3.opExtrude","SWEPT_EDGE",EDGE,{"disambiguationData":[OSD([subQ5,subQ4])]})});}
            var Q3;
            {var subQ31=sQuery(id+"F0.wireOp",EDGE,"ZneDm9bx-5IyB-59Bp-oYEK-Q0VNZlboGKRZ");var subQ33=sQuery(id+"F0.wireOp",EDGE,"2L4el6af-6clv-Qu9y-48nY-g4NLMY6r5mmJ.bottom");var subQ35=sQuery(id+"F0.wireOp",EDGE,"E2.sketch_text.stroke-70");var subQ36=sQuery(id+"F0.wireOp",EDGE,"E2.sketch_text.stroke-69");var subQ37=sQuery(id+"F0.wireOp",EDGE,"E2.sketch_text.stroke-68");var subQ38=sQuery(id+"F0.wireOp",EDGE,"E2.sketch_text.stroke-67");Q3=makeQuery(id+"F4.boolean.opBoolean","SPLIT",EDGE,{"disambiguationData":[TD([makeQuery(id+"F2.opExtrude","CAP_FACE",FACE,{"disambiguationData":[OSD([subQ38,subQ37,subQ36,subQ35])],"isStart":true})])],"derivedFrom":makeQuery(id+"F3.opExtrude","SWEPT_EDGE",EDGE,{"disambiguationData":[OSD([subQ33,subQ31])]})});}
            var Q4;
            {var subQ0=sQuery(id+"F0.wireOp",EDGE,"E1.top");Q4=makeQuery(id+"F4.boolean.opBoolean","MERGE",FACE,{"derivedFrom":[makeQuery(id+"F1.opExtrude","SWEPT_FACE",FACE,{"disambiguationData":[OSD([subQ0])]}),makeQuery(id+"F4.opExtrude","SWEPT_FACE",FACE,{"disambiguationData":[OSD([subQ0]),TDD([makeQuery(id+"F0.imprint","IMPRINT",EDGE,{"disambiguationData":[TD([[makeQuery(id+"F0.imprint","INTERSECT",VERTEX,{"derivedFrom":[subQ0,sQuery(id+"F0.wireOp",EDGE,"E1.left")]}),-1.0]])],"derivedFrom":subQ0})])]}),makeQuery(id+"F4.opExtrude","SWEPT_FACE",FACE,{"disambiguationData":[OSD([subQ0]),TDD([makeQuery(id+"F0.imprint","IMPRINT",EDGE,{"disambiguationData":[TD([[makeQuery(id+"F0.imprint","INTERSECT",VERTEX,{"derivedFrom":[subQ0,sQuery(id+"F0.wireOp",EDGE,"E1.right")]}),1.0]])],"derivedFrom":subQ0})])]})]});}
            fillet(context, id + "F7", {"entities" : qUnion([Q0, Q1, Q2, Q3, Q4]), "radius" : 2 * mm, "tangentPropagation" : true, "allowEdgeOverflow" : false});
        }
        {
            var Q0;
            {var subQ0=sQuery(id+"F0.wireOp",EDGE,"E0.bottom");var subQ1=makeQuery(id+"F0.imprint","INTERSECT",VERTEX,{"derivedFrom":[subQ0,sQuery(id+"F0.wireOp",EDGE,"E1.left")]});Q0=makeQuery(id+"F3.boolean.opBoolean","MERGE",FACE,{"derivedFrom":[makeQuery(id+"F1.opExtrude","SWEPT_FACE",FACE,{"disambiguationData":[OSD([subQ0]),TDD([makeQuery(id+"F0.imprint","IMPRINT",EDGE,{"disambiguationData":[TD([[makeQuery(id+"F0.imprint","INTERSECT",VERTEX,{"derivedFrom":[subQ0,sQuery(id+"F0.wireOp",EDGE,"E0.left")]}),-1.0]])],"derivedFrom":subQ0})])]}),makeQuery(id+"F3.opExtrude","SWEPT_FACE",FACE,{"disambiguationData":[OSD([subQ0]),TDD([makeQuery(id+"F0.imprint","IMPRINT",EDGE,{"disambiguationData":[TD([[subQ1,-1.0]])],"derivedFrom":subQ0})])]})]});}
            var Q1;
            {var subQ0=sQuery(id+"F0.wireOp",EDGE,"E0.bottom");var subQ1=makeQuery(id+"F0.imprint","INTERSECT",VERTEX,{"derivedFrom":[subQ0,sQuery(id+"F0.wireOp",EDGE,"E1.right")]});Q1=makeQuery(id+"F3.boolean.opBoolean","MERGE",FACE,{"derivedFrom":[makeQuery(id+"F1.opExtrude","SWEPT_FACE",FACE,{"disambiguationData":[OSD([subQ0]),TDD([makeQuery(id+"F0.imprint","IMPRINT",EDGE,{"disambiguationData":[TD([[makeQuery(id+"F0.imprint","INTERSECT",VERTEX,{"derivedFrom":[subQ0,sQuery(id+"F0.wireOp",EDGE,"E0.right")]}),1.0]])],"derivedFrom":subQ0})])]}),makeQuery(id+"F3.opExtrude","SWEPT_FACE",FACE,{"disambiguationData":[OSD([subQ0]),TDD([makeQuery(id+"F0.imprint","IMPRINT",EDGE,{"disambiguationData":[TD([[subQ1,1.0]])],"derivedFrom":subQ0})])]})]});}
            fillet(context, id + "F8", {"entities" : qUnion([Q0, Q1]), "radius" : 2 * mm, "tangentPropagation" : true, "allowEdgeOverflow" : false});
        }
    });
